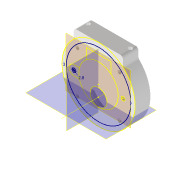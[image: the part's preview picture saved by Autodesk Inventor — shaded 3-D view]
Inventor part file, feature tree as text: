
AUTODESK INVENTOR PART (.ipt)
format: ipt  version: 2022.5 (Build 265521000, 521)  size: 299,520 bytes
history: native  units: mm
features: reference x21, sketch x9, other x7, plane x4, extrude x4, projected_geometry x4, hole x3, revolve x1
ambient origin geometry x8: Origin, YZ Plane, XZ Plane, XY Plane, X Axis, Y Axis, Z Axis, Center Point
bodies: Volumenkörper1 (feature_tree)
feature tree (53):
  plane  "Arbeitsebene1"
  extrude  "Extrusion1"  Depth=2.8mm
  sketch  "Skizze2"  dims[d2=2.8mm d3=12.0mm]
  plane  "Arbeitsebene2"
  extrude  "Extrusion3"  Depth=12.0mm
  plane  "Arbeitsebene4"
  revolve  "Umdrehung1"
  extrude  "Extrusion5"  Depth=3.0mm
  hole  "Bohrung1"  [1 undecoded]
  extrude  "Extrusion6"  Depth=0.872665mm
  hole  "Bohrung2"  [1 undecoded]
  hole  "Bohrung3"  [1 undecoded]
  sketch  "Skizze1"  dims[d0=52.0mm d1=2.8mm]
  reference  "Referenz1"
  reference  "Referenz2"
  reference  "Referenz3"
  reference  "Referenz4"
  projected_geometry  "Projizierte Kontur1"
  reference  "Referenz5"
  reference  "Referenz6"
  reference  "Referenz7"
  reference  "Referenz8"
  reference  "Referenz9"
  reference  "Referenz10"
  reference  "Referenz11"
  reference  "Referenz12"
  sketch  "Skizze3"  dims[d4=1.0mm d5=0.0mm d6=3.0mm]
  plane  "Arbeitsebene3"
  other  "Arbeitsachse1"
  sketch  "Skizze4"  dims[d9=2.8mm d10=36.0mm]
  projected_geometry  "Projizierte Kontur2"
  sketch  "Skizze7"  dims[d11=0.872665mm d12=0.872665mm]
  projected_geometry  "Projizierte Kontur3"
  sketch  "Skizze8"  dims[d13=10.0mm d14=0.0mm d15=90.0deg]
  projected_geometry  "Projizierte Kontur4"
  sketch  "Skizze9"  dims[d16=2.8mm d17=0.0mm]
  reference  "Referenz13"
  reference  "Referenz14"
  reference  "Referenz15"
  sketch  "Skizze10"  dims[d18=180.0deg]
  reference  "Referenz16"
  reference  "Referenz17"
  sketch  "Skizze11"  dims[d28=2.0mm d29=3.0mm d30=4.0mm d31=4.0mm d32=0.0mm d33=0.0mm d34=3.0mm d35=6.0mm d36=4.0mm d37=2.0mm d38=90.0deg d39=8.0mm d40=20.594885mm d41=10.0mm d42=0.0mm d43=25.0mm d44=2.8mm d45=6.0mm d46=4.0mm d47=2.0mm d48=90.0deg d49=8.0mm d50=20.594885mm d51=2.8mm d52=6.0mm d53=6.5mm d54=3.5mm d55=90.0deg d56=30.0mm d57=20.594885mm]
  reference  "Referenz18"
  reference  "Referenz19"
  reference  "Referenz20"
  reference  "Referenz21"
  other  "Planktoscope_Mini_Peristalticpump_new.iam"
  other  "00_Stepper_Motor_28BYJ-48:1"
  other  "Pump_Base_Motor_new:1"
  other  "Assembly_Matchboxscope_injectionmolded_xiao:1"
  other  "IM_Matchboxscope_plate:1"
  other  "IM_Matchboxscope_base_xiao_lid:1"
note: 3 required parameter values undecoded (feature->parameter linkage not recoverable at this tier; creation-order binding heuristic only, values carry confidence <= 0.55)
